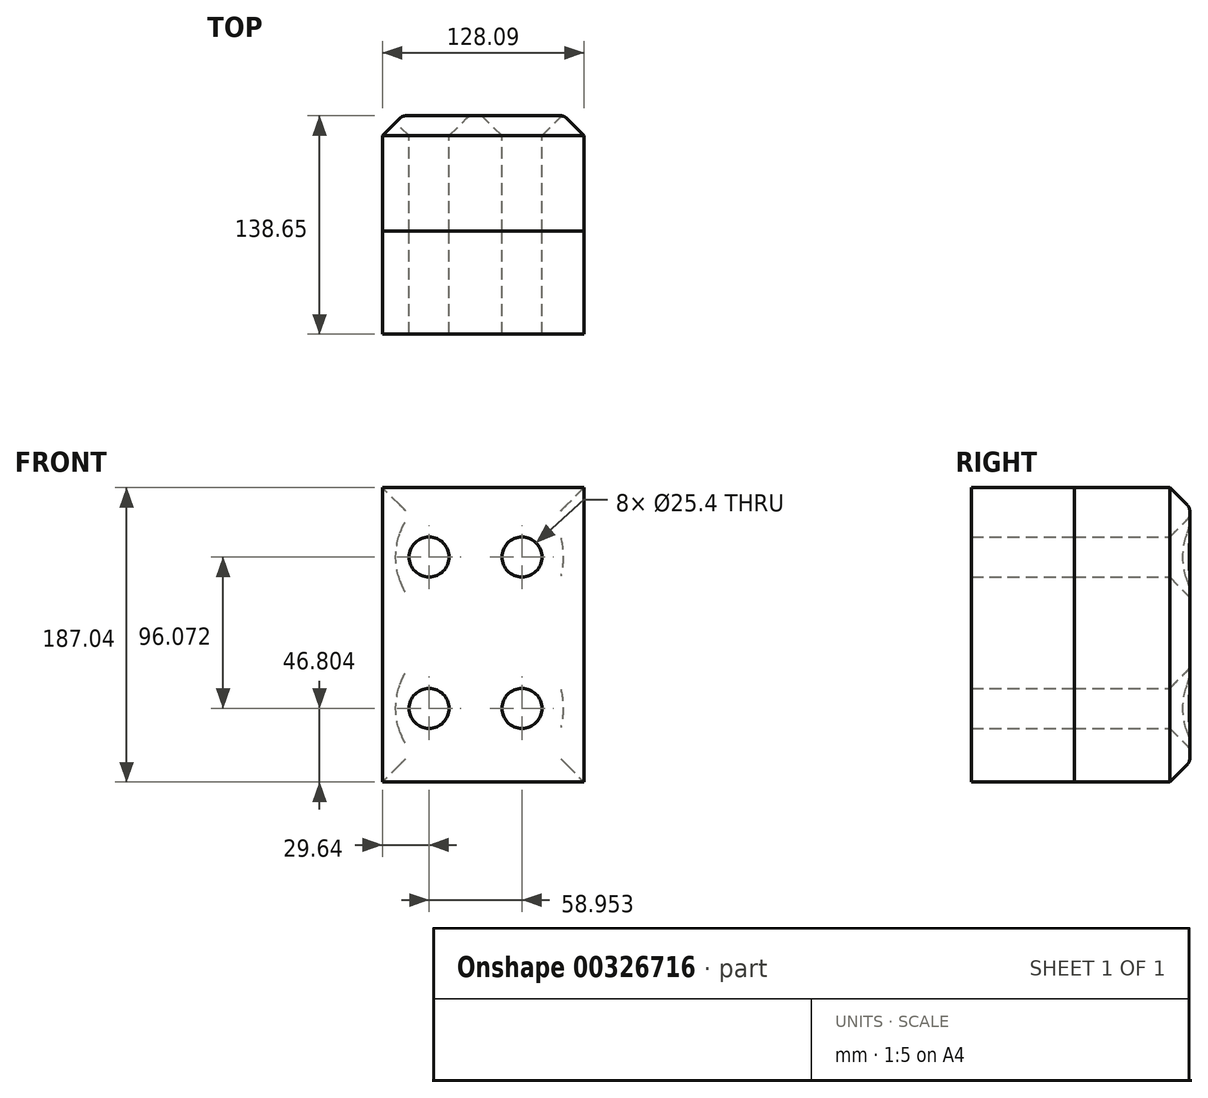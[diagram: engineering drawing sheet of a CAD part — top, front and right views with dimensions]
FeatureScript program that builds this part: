
annotation { "Feature Type Name" : "Feature", "Feature Type Description" : "" }
export const myFeature = defineFeature(function(context is Context, id is Id, definition is map)
    precondition{}
    {
        {
            var Q0;
            Q0=qCreatedBy(makeId("Front.planeOp"),FACE);
            var sketch = newSketch(context, id + "F0", { "sketchPlane" : qUnion([Q0])});
            skLineSegment(sketch, "E0.bottom", {"start": v(-66.47, 93.39) * mm, "end": v(61.62, 93.39) * mm});
            skLineSegment(sketch, "E0.top", {"start": v(-66.47, -93.65) * mm, "end": v(61.62, -93.65) * mm});
            skLineSegment(sketch, "E0.left", {"start": v(-66.47, 93.39) * mm, "end": v(-66.47, -93.65) * mm});
            skLineSegment(sketch, "E0.right", {"start": v(61.62, 93.39) * mm, "end": v(61.62, -93.65) * mm});
            skSolve(sketch);
        }
        {
            var Q0;
            Q0=makeQuery(id+"F0.imprint","IMPRINT",FACE,{"disambiguationData":[TD([[makeQuery(id+"F0.imprint","IMPRINT",EDGE,{"derivedFrom":sQuery(id+"F0.wireOp",EDGE,"E0.bottom")}),-1.0]])]});
            var sketch = newSketch(context, id + "F1", { "sketchPlane" : qUnion([Q0])});
            skSolve(sketch);
        }
        {
            var Q0;
            Q0 = qSketchRegion(id + "F1", true);
            var Q1;
            Q1=makeQuery(id+"F0.imprint","IMPRINT",FACE,{"disambiguationData":[TD([[makeQuery(id+"F0.imprint","IMPRINT",EDGE,{"derivedFrom":sQuery(id+"F0.wireOp",EDGE,"E0.bottom")}),-1.0]])]});
            var Q2;
            Q2=makeQuery(id+"F1.imprint","IMPRINT",FACE,{"disambiguationData":[TD([[makeQuery(id+"F1.imprint","IMPRINT",EDGE,{"derivedFrom":makeQuery(id+"F0.imprint","IMPRINT",EDGE,{"derivedFrom":sQuery(id+"F0.wireOp",EDGE,"E0.bottom")})}),-1.0]])]});
            extrude(context, id + "F2", {"entities" : qUnion([Q0, Q1, Q2]), "depth" : 65.35 * mm});
        }
        {
            var Q0;
            {var subQ0=sQuery(id+"F0.wireOp",EDGE,"E0.right");var subQ1=sQuery(id+"F0.wireOp",EDGE,"E0.left");var subQ2=sQuery(id+"F0.wireOp",EDGE,"E0.top");var subQ3=sQuery(id+"F0.wireOp",EDGE,"E0.bottom");Q0=makeQuery(id+"F2.opExtrude","CAP_FACE",FACE,{"disambiguationData":[OSD([subQ3,subQ2,subQ1,subQ0]),TDD([makeQuery(id+"F1.imprint","IMPRINT",EDGE,{"derivedFrom":makeQuery(id+"F0.imprint","IMPRINT",EDGE,{"derivedFrom":subQ3})}),makeQuery(id+"F1.imprint","IMPRINT",EDGE,{"derivedFrom":makeQuery(id+"F0.imprint","IMPRINT",EDGE,{"derivedFrom":subQ2})}),makeQuery(id+"F1.imprint","IMPRINT",EDGE,{"derivedFrom":makeQuery(id+"F0.imprint","IMPRINT",EDGE,{"derivedFrom":subQ1})}),makeQuery(id+"F1.imprint","IMPRINT",EDGE,{"derivedFrom":makeQuery(id+"F0.imprint","IMPRINT",EDGE,{"derivedFrom":subQ0})})])],"isStart":true});}
            extrude(context, id + "F3", {"entities" : qUnion([Q0]), "depth" : 73.3 * mm});
        }
        {
            var Q0;
            Q0=makeQuery(id+"F3.opExtrude","CAP_FACE",FACE,{"disambiguationData":[OSD([sQuery(id+"F0.wireOp",EDGE,"E0.bottom"),sQuery(id+"F0.wireOp",EDGE,"E0.top"),sQuery(id+"F0.wireOp",EDGE,"E0.left"),sQuery(id+"F0.wireOp",EDGE,"E0.right")])],"isStart":false});
            var sketch = newSketch(context, id + "F4", { "sketchPlane" : qUnion([Q0])});
            skPoint(sketch, "E1", {"position": v(-22.12, 49.23) * mm});
            skPoint(sketch, "E2", {"position": v(-22.12, -46.85) * mm});
            skPoint(sketch, "E3", {"position": v(36.83, -46.85) * mm});
            skPoint(sketch, "E4", {"position": v(36.83, 49.23) * mm});
            skSolve(sketch);
        }
        {
            var Q0;
            Q0=sQuery(id+"F4.wireOp",VERTEX,"E3");
            var Q1;
            Q1=sQuery(id+"F4.wireOp",VERTEX,"E4");
            var Q2;
            Q2=sQuery(id+"F4.wireOp",VERTEX,"E1");
            var Q3;
            Q3=sQuery(id+"F4.wireOp",VERTEX,"E2");
            var Q4;
            {var subQ0=sQuery(id+"F0.wireOp",EDGE,"E0.right");var subQ1=sQuery(id+"F0.wireOp",EDGE,"E0.left");var subQ2=sQuery(id+"F0.wireOp",EDGE,"E0.top");var subQ3=sQuery(id+"F0.wireOp",EDGE,"E0.bottom");Q4=makeQuery(id+"F2.opExtrude","SWEPT_BODY",BODY,{"disambiguationData":[OSD([subQ3,subQ2,subQ1,subQ0]),TDD([makeQuery(id+"F0.imprint","IMPRINT",EDGE,{"derivedFrom":subQ3}),makeQuery(id+"F0.imprint","IMPRINT",EDGE,{"derivedFrom":subQ2}),makeQuery(id+"F0.imprint","IMPRINT",EDGE,{"derivedFrom":subQ1}),makeQuery(id+"F0.imprint","IMPRINT",EDGE,{"derivedFrom":subQ0})])]});}
            var Q5;
            {var subQ0=sQuery(id+"F0.wireOp",EDGE,"E0.right");var subQ1=sQuery(id+"F0.wireOp",EDGE,"E0.left");var subQ2=sQuery(id+"F0.wireOp",EDGE,"E0.top");var subQ3=sQuery(id+"F0.wireOp",EDGE,"E0.bottom");Q5=makeQuery(id+"F2.opExtrude","SWEPT_BODY",BODY,{"disambiguationData":[OSD([subQ3,subQ2,subQ1,subQ0]),TDD([makeQuery(id+"F1.imprint","IMPRINT",EDGE,{"derivedFrom":makeQuery(id+"F0.imprint","IMPRINT",EDGE,{"derivedFrom":subQ3})}),makeQuery(id+"F1.imprint","IMPRINT",EDGE,{"derivedFrom":makeQuery(id+"F0.imprint","IMPRINT",EDGE,{"derivedFrom":subQ2})}),makeQuery(id+"F1.imprint","IMPRINT",EDGE,{"derivedFrom":makeQuery(id+"F0.imprint","IMPRINT",EDGE,{"derivedFrom":subQ1})}),makeQuery(id+"F1.imprint","IMPRINT",EDGE,{"derivedFrom":makeQuery(id+"F0.imprint","IMPRINT",EDGE,{"derivedFrom":subQ0})})])]});}
            var Q6;
            Q6=makeQuery(id+"F3.opExtrude","SWEPT_BODY",BODY,{"disambiguationData":[OSD([sQuery(id+"F0.wireOp",EDGE,"E0.bottom"),sQuery(id+"F0.wireOp",EDGE,"E0.top"),sQuery(id+"F0.wireOp",EDGE,"E0.left"),sQuery(id+"F0.wireOp",EDGE,"E0.right")])]});
            hole(context, id + "F5", {"style" : HoleStyle.SIMPLE, "endStyle" : HoleEndStyle.THROUGH, "holeDiameter" : 25.4 * mm, "tappedDepth" : 12.7 * mm, "tapClearance" : 3, "locations" : qUnion([Q0, Q1, Q2, Q3]), "scope" : qUnion([Q4, Q5, Q6])});
        }
        {
            var Q0;
            Q0=makeQuery(id+"F5.hole-1.boolean.opBoolean","COPY",EDGE,{"derivedFrom":makeQuery(id+"F5.hole-1.opRevolve","SWEPT_EDGE",EDGE,{"disambiguationData":[OSD([sQuery(id+"F5.hole-1.sketch.wireOp",EDGE,"core_line_2"),sQuery(id+"F5.hole-1.sketch.wireOp",EDGE,"core_line_3")])]})});
            var Q1;
            Q1=makeQuery(id+"F5.hole-2.boolean.opBoolean","COPY",EDGE,{"derivedFrom":makeQuery(id+"F5.hole-2.opRevolve","SWEPT_EDGE",EDGE,{"disambiguationData":[OSD([sQuery(id+"F5.hole-2.sketch.wireOp",EDGE,"core_line_2"),sQuery(id+"F5.hole-2.sketch.wireOp",EDGE,"core_line_3")])]})});
            var Q2;
            Q2=makeQuery(id+"F5.hole-3.boolean.opBoolean","COPY",EDGE,{"derivedFrom":makeQuery(id+"F5.hole-3.opRevolve","SWEPT_EDGE",EDGE,{"disambiguationData":[OSD([sQuery(id+"F5.hole-3.sketch.wireOp",EDGE,"core_line_2"),sQuery(id+"F5.hole-3.sketch.wireOp",EDGE,"core_line_3")])]})});
            var Q3;
            Q3=makeQuery(id+"F5.hole-0.boolean.opBoolean","COPY",EDGE,{"derivedFrom":makeQuery(id+"F5.hole-0.opRevolve","SWEPT_EDGE",EDGE,{"disambiguationData":[OSD([sQuery(id+"F5.hole-0.sketch.wireOp",EDGE,"core_line_2"),sQuery(id+"F5.hole-0.sketch.wireOp",EDGE,"core_line_3")])]})});
            var Q4;
            Q4=makeQuery(id+"F3.opExtrude","CAP_EDGE",EDGE,{"disambiguationData":[OSD([sQuery(id+"F0.wireOp",EDGE,"E0.right")])],"isStart":false});
            var Q5;
            Q5=makeQuery(id+"F3.opExtrude","CAP_FACE",FACE,{"disambiguationData":[OSD([sQuery(id+"F0.wireOp",EDGE,"E0.bottom"),sQuery(id+"F0.wireOp",EDGE,"E0.top"),sQuery(id+"F0.wireOp",EDGE,"E0.left"),sQuery(id+"F0.wireOp",EDGE,"E0.right")])],"isStart":false});
            chamfer(context, id + "F6", {"entities" : qUnion([Q0, Q1, Q2, Q3, Q4, Q5]), "width" : 12.7 * mm, "tangentPropagation" : true});
        }
        {
            var Q0;
            Q0=makeQuery(id+"F6.opChamfer","BLEND_EDGE",EDGE,{"blendedFrom":[makeQuery(id+"F3.opExtrude","CAP_EDGE",EDGE,{"disambiguationData":[OSD([sQuery(id+"F0.wireOp",EDGE,"E0.left")])],"isStart":false}),makeQuery(id+"F5.hole-0.boolean.opBoolean","COPY",EDGE,{"derivedFrom":makeQuery(id+"F5.hole-0.opRevolve","SWEPT_EDGE",EDGE,{"disambiguationData":[OSD([sQuery(id+"F5.hole-0.sketch.wireOp",EDGE,"core_line_2"),sQuery(id+"F5.hole-0.sketch.wireOp",EDGE,"core_line_3")])]})})],"blendedInto":[]});
            var Q1;
            {var subQ0=sQuery(id+"F0.wireOp",EDGE,"E0.left");Q1=makeQuery(id+"F6.opChamfer","BLEND_EDGE",EDGE,{"disambiguationData":[OD(2.0)],"blendedFrom":[makeQuery(id+"F3.opExtrude","CAP_EDGE",EDGE,{"disambiguationData":[OSD([subQ0])],"isStart":false}),makeQuery(id+"F3.opExtrude","CAP_FACE",FACE,{"disambiguationData":[OSD([sQuery(id+"F0.wireOp",EDGE,"E0.bottom"),sQuery(id+"F0.wireOp",EDGE,"E0.top"),subQ0,sQuery(id+"F0.wireOp",EDGE,"E0.right")])],"isStart":false})],"blendedInto":[makeQuery(id+"F3.opExtrude","CAP_FACE",FACE,{"disambiguationData":[OSD([sQuery(id+"F0.wireOp",EDGE,"E0.bottom"),sQuery(id+"F0.wireOp",EDGE,"E0.top"),subQ0,sQuery(id+"F0.wireOp",EDGE,"E0.right")])],"isStart":false})]});}
            var Q2;
            Q2=makeQuery(id+"F6.opChamfer","BLEND_EDGE",EDGE,{"blendedFrom":[makeQuery(id+"F5.hole-0.boolean.opBoolean","COPY",EDGE,{"derivedFrom":makeQuery(id+"F5.hole-0.opRevolve","SWEPT_EDGE",EDGE,{"disambiguationData":[OSD([sQuery(id+"F5.hole-0.sketch.wireOp",EDGE,"core_line_2"),sQuery(id+"F5.hole-0.sketch.wireOp",EDGE,"core_line_3")])]})}),makeQuery(id+"F3.opExtrude","CAP_FACE",FACE,{"disambiguationData":[OSD([sQuery(id+"F0.wireOp",EDGE,"E0.bottom"),sQuery(id+"F0.wireOp",EDGE,"E0.top"),sQuery(id+"F0.wireOp",EDGE,"E0.left"),sQuery(id+"F0.wireOp",EDGE,"E0.right")])],"isStart":false})],"blendedInto":[makeQuery(id+"F3.opExtrude","CAP_FACE",FACE,{"disambiguationData":[OSD([sQuery(id+"F0.wireOp",EDGE,"E0.bottom"),sQuery(id+"F0.wireOp",EDGE,"E0.top"),sQuery(id+"F0.wireOp",EDGE,"E0.left"),sQuery(id+"F0.wireOp",EDGE,"E0.right")])],"isStart":false})]});
            var Q3;
            Q3=makeQuery(id+"F6.opChamfer","BLEND_EDGE",EDGE,{"blendedFrom":[makeQuery(id+"F5.hole-3.boolean.opBoolean","COPY",EDGE,{"derivedFrom":makeQuery(id+"F5.hole-3.opRevolve","SWEPT_EDGE",EDGE,{"disambiguationData":[OSD([sQuery(id+"F5.hole-3.sketch.wireOp",EDGE,"core_line_2"),sQuery(id+"F5.hole-3.sketch.wireOp",EDGE,"core_line_3")])]})}),makeQuery(id+"F3.opExtrude","CAP_FACE",FACE,{"disambiguationData":[OSD([sQuery(id+"F0.wireOp",EDGE,"E0.bottom"),sQuery(id+"F0.wireOp",EDGE,"E0.top"),sQuery(id+"F0.wireOp",EDGE,"E0.left"),sQuery(id+"F0.wireOp",EDGE,"E0.right")])],"isStart":false})],"blendedInto":[makeQuery(id+"F3.opExtrude","CAP_FACE",FACE,{"disambiguationData":[OSD([sQuery(id+"F0.wireOp",EDGE,"E0.bottom"),sQuery(id+"F0.wireOp",EDGE,"E0.top"),sQuery(id+"F0.wireOp",EDGE,"E0.left"),sQuery(id+"F0.wireOp",EDGE,"E0.right")])],"isStart":false})]});
            var Q4;
            {var subQ0=sQuery(id+"F0.wireOp",EDGE,"E0.right");Q4=makeQuery(id+"F6.opChamfer","BLEND_EDGE",EDGE,{"blendedFrom":[makeQuery(id+"F3.opExtrude","CAP_EDGE",EDGE,{"disambiguationData":[OSD([subQ0])],"isStart":false}),makeQuery(id+"F3.opExtrude","CAP_FACE",FACE,{"disambiguationData":[OSD([sQuery(id+"F0.wireOp",EDGE,"E0.bottom"),sQuery(id+"F0.wireOp",EDGE,"E0.top"),sQuery(id+"F0.wireOp",EDGE,"E0.left"),subQ0])],"isStart":false})],"blendedInto":[makeQuery(id+"F3.opExtrude","CAP_FACE",FACE,{"disambiguationData":[OSD([sQuery(id+"F0.wireOp",EDGE,"E0.bottom"),sQuery(id+"F0.wireOp",EDGE,"E0.top"),sQuery(id+"F0.wireOp",EDGE,"E0.left"),subQ0])],"isStart":false})]});}
            var Q5;
            Q5=makeQuery(id+"F3.opExtrude","CAP_FACE",FACE,{"disambiguationData":[OSD([sQuery(id+"F0.wireOp",EDGE,"E0.bottom"),sQuery(id+"F0.wireOp",EDGE,"E0.top"),sQuery(id+"F0.wireOp",EDGE,"E0.left"),sQuery(id+"F0.wireOp",EDGE,"E0.right")])],"isStart":false});
            var Q6;
            Q6=makeQuery(id+"F6.opChamfer","BLEND_EDGE",EDGE,{"blendedFrom":[makeQuery(id+"F3.opExtrude","CAP_EDGE",EDGE,{"disambiguationData":[OSD([sQuery(id+"F0.wireOp",EDGE,"E0.left")])],"isStart":false}),makeQuery(id+"F5.hole-1.boolean.opBoolean","COPY",EDGE,{"derivedFrom":makeQuery(id+"F5.hole-1.opRevolve","SWEPT_EDGE",EDGE,{"disambiguationData":[OSD([sQuery(id+"F5.hole-1.sketch.wireOp",EDGE,"core_line_2"),sQuery(id+"F5.hole-1.sketch.wireOp",EDGE,"core_line_3")])]})})],"blendedInto":[]});
            var Q7;
            {var subQ0=sQuery(id+"F0.wireOp",EDGE,"E0.right");var subQ1=sQuery(id+"F0.wireOp",EDGE,"E0.left");var subQ2=sQuery(id+"F0.wireOp",EDGE,"E0.top");var subQ3=sQuery(id+"F0.wireOp",EDGE,"E0.bottom");var subQ4=sQuery(id+"F5.hole-1.sketch.wireOp",EDGE,"core_line_2");Q7=makeQuery(id+"F6.opChamfer","BLEND_EDGE",EDGE,{"blendedFrom":[makeQuery(id+"F5.hole-1.boolean.opBoolean","COPY",EDGE,{"derivedFrom":makeQuery(id+"F5.hole-1.opRevolve","SWEPT_EDGE",EDGE,{"disambiguationData":[OSD([subQ4,sQuery(id+"F5.hole-1.sketch.wireOp",EDGE,"core_line_3")])]})}),makeQuery(id+"F5.hole-1.boolean.opBoolean","COPY",FACE,{"disambiguationData":[TD([makeQuery(id+"F3.opExtrude","CAP_FACE",FACE,{"disambiguationData":[OSD([subQ3,subQ2,subQ1,subQ0])],"isStart":true})])],"derivedFrom":makeQuery(id+"F5.hole-1.opRevolve","SWEPT_FACE",FACE,{"disambiguationData":[OSD([subQ4])]})})],"blendedInto":[makeQuery(id+"F5.hole-1.boolean.opBoolean","COPY",FACE,{"disambiguationData":[TD([makeQuery(id+"F3.opExtrude","CAP_FACE",FACE,{"disambiguationData":[OSD([subQ3,subQ2,subQ1,subQ0])],"isStart":true})])],"derivedFrom":makeQuery(id+"F5.hole-1.opRevolve","SWEPT_FACE",FACE,{"disambiguationData":[OSD([subQ4])]})})]});}
            var Q8;
            {var subQ0=sQuery(id+"F0.wireOp",EDGE,"E0.right");var subQ1=sQuery(id+"F0.wireOp",EDGE,"E0.left");var subQ2=sQuery(id+"F0.wireOp",EDGE,"E0.top");var subQ3=sQuery(id+"F0.wireOp",EDGE,"E0.bottom");var subQ4=sQuery(id+"F5.hole-2.sketch.wireOp",EDGE,"core_line_2");Q8=makeQuery(id+"F6.opChamfer","BLEND_EDGE",EDGE,{"blendedFrom":[makeQuery(id+"F5.hole-2.boolean.opBoolean","COPY",EDGE,{"derivedFrom":makeQuery(id+"F5.hole-2.opRevolve","SWEPT_EDGE",EDGE,{"disambiguationData":[OSD([subQ4,sQuery(id+"F5.hole-2.sketch.wireOp",EDGE,"core_line_3")])]})}),makeQuery(id+"F5.hole-2.boolean.opBoolean","COPY",FACE,{"disambiguationData":[TD([makeQuery(id+"F3.opExtrude","CAP_FACE",FACE,{"disambiguationData":[OSD([subQ3,subQ2,subQ1,subQ0])],"isStart":true})])],"derivedFrom":makeQuery(id+"F5.hole-2.opRevolve","SWEPT_FACE",FACE,{"disambiguationData":[OSD([subQ4])]})})],"blendedInto":[makeQuery(id+"F5.hole-2.boolean.opBoolean","COPY",FACE,{"disambiguationData":[TD([makeQuery(id+"F3.opExtrude","CAP_FACE",FACE,{"disambiguationData":[OSD([subQ3,subQ2,subQ1,subQ0])],"isStart":true})])],"derivedFrom":makeQuery(id+"F5.hole-2.opRevolve","SWEPT_FACE",FACE,{"disambiguationData":[OSD([subQ4])]})})]});}
            var Q9;
            {var subQ0=sQuery(id+"F0.wireOp",EDGE,"E0.right");var subQ1=sQuery(id+"F0.wireOp",EDGE,"E0.left");var subQ2=sQuery(id+"F0.wireOp",EDGE,"E0.top");var subQ3=sQuery(id+"F0.wireOp",EDGE,"E0.bottom");var subQ4=sQuery(id+"F5.hole-3.sketch.wireOp",EDGE,"core_line_2");Q9=makeQuery(id+"F6.opChamfer","BLEND_EDGE",EDGE,{"blendedFrom":[makeQuery(id+"F5.hole-3.boolean.opBoolean","COPY",EDGE,{"derivedFrom":makeQuery(id+"F5.hole-3.opRevolve","SWEPT_EDGE",EDGE,{"disambiguationData":[OSD([subQ4,sQuery(id+"F5.hole-3.sketch.wireOp",EDGE,"core_line_3")])]})}),makeQuery(id+"F5.hole-3.boolean.opBoolean","COPY",FACE,{"disambiguationData":[TD([makeQuery(id+"F3.opExtrude","CAP_FACE",FACE,{"disambiguationData":[OSD([subQ3,subQ2,subQ1,subQ0])],"isStart":true})])],"derivedFrom":makeQuery(id+"F5.hole-3.opRevolve","SWEPT_FACE",FACE,{"disambiguationData":[OSD([subQ4])]})})],"blendedInto":[makeQuery(id+"F5.hole-3.boolean.opBoolean","COPY",FACE,{"disambiguationData":[TD([makeQuery(id+"F3.opExtrude","CAP_FACE",FACE,{"disambiguationData":[OSD([subQ3,subQ2,subQ1,subQ0])],"isStart":true})])],"derivedFrom":makeQuery(id+"F5.hole-3.opRevolve","SWEPT_FACE",FACE,{"disambiguationData":[OSD([subQ4])]})})]});}
            var Q10;
            {var subQ0=sQuery(id+"F0.wireOp",EDGE,"E0.right");var subQ1=sQuery(id+"F0.wireOp",EDGE,"E0.left");var subQ2=sQuery(id+"F0.wireOp",EDGE,"E0.top");var subQ3=sQuery(id+"F0.wireOp",EDGE,"E0.bottom");var subQ4=sQuery(id+"F5.hole-0.sketch.wireOp",EDGE,"core_line_2");Q10=makeQuery(id+"F6.opChamfer","BLEND_EDGE",EDGE,{"blendedFrom":[makeQuery(id+"F5.hole-0.boolean.opBoolean","COPY",EDGE,{"derivedFrom":makeQuery(id+"F5.hole-0.opRevolve","SWEPT_EDGE",EDGE,{"disambiguationData":[OSD([subQ4,sQuery(id+"F5.hole-0.sketch.wireOp",EDGE,"core_line_3")])]})}),makeQuery(id+"F5.hole-0.boolean.opBoolean","COPY",FACE,{"disambiguationData":[TD([makeQuery(id+"F3.opExtrude","CAP_FACE",FACE,{"disambiguationData":[OSD([subQ3,subQ2,subQ1,subQ0])],"isStart":true})])],"derivedFrom":makeQuery(id+"F5.hole-0.opRevolve","SWEPT_FACE",FACE,{"disambiguationData":[OSD([subQ4])]})})],"blendedInto":[makeQuery(id+"F5.hole-0.boolean.opBoolean","COPY",FACE,{"disambiguationData":[TD([makeQuery(id+"F3.opExtrude","CAP_FACE",FACE,{"disambiguationData":[OSD([subQ3,subQ2,subQ1,subQ0])],"isStart":true})])],"derivedFrom":makeQuery(id+"F5.hole-0.opRevolve","SWEPT_FACE",FACE,{"disambiguationData":[OSD([subQ4])]})})]});}
            fillet(context, id + "F7", {"entities" : qUnion([Q0, Q1, Q2, Q3, Q4, Q5, Q6, Q7, Q8, Q9, Q10]), "radius" : 5.08 * mm, "tangentPropagation" : true, "allowEdgeOverflow" : false});
        }
    });
